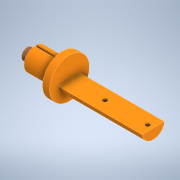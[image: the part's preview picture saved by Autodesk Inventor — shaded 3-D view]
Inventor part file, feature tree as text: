
AUTODESK INVENTOR PART (.ipt)
format: ipt  version: 2021 (Build 250183000, 183)  size: 155,648 bytes
history: native  units: mm
features: sketch x4, other x2, extrude x2, hole x1, thread x1, fillet x1
ambient origin geometry x8: Origin, YZ Plane, XZ Plane, XY Plane, X Axis, Y Axis, Z Axis, Center Point
bodies: Body1 (feature_tree)
feature tree (11):
  other  "Sólido1"
  other  "Revolução1"
  extrude  "Extrusão1"  Depth=5.0mm
  hole  "Furo1"  [1 undecoded]
  thread  "Rosca1"  [1 undecoded]
  fillet  "Arredondamento1"  Radius=6.0mm
  extrude  "Extrusão2"  Depth=10.0mm TaperAngle=0.0deg
  sketch  "Esboço1"  dims[d2=6.0mm d3=5.0mm]
  sketch  "Esboço2"  dims[d4=6.0mm d5=19.0mm d6=4.0mm d7=6.0mm]
  sketch  "Esboço3"  dims[d8=90.0deg d9=10.0mm d10=1.0mm d11=0.0mm d12=0.0mm]
  sketch  "Esboço4"  dims[d13=25.0mm d14=30.0mm d15=3.0mm d16=6.0mm d17=4.0mm d18=2.0mm d19=90.0deg d20=8.0mm d21=20.594885mm d22=7.0mm d23=0.0mm d24=0.2mm d25=0.6mm d26=1.4mm d27=0.6mm d28=1.4mm d29=14.0mm d30=0.0mm]
note: 2 required parameter values undecoded (feature->parameter linkage not recoverable at this tier; creation-order binding heuristic only, values carry confidence <= 0.55)
